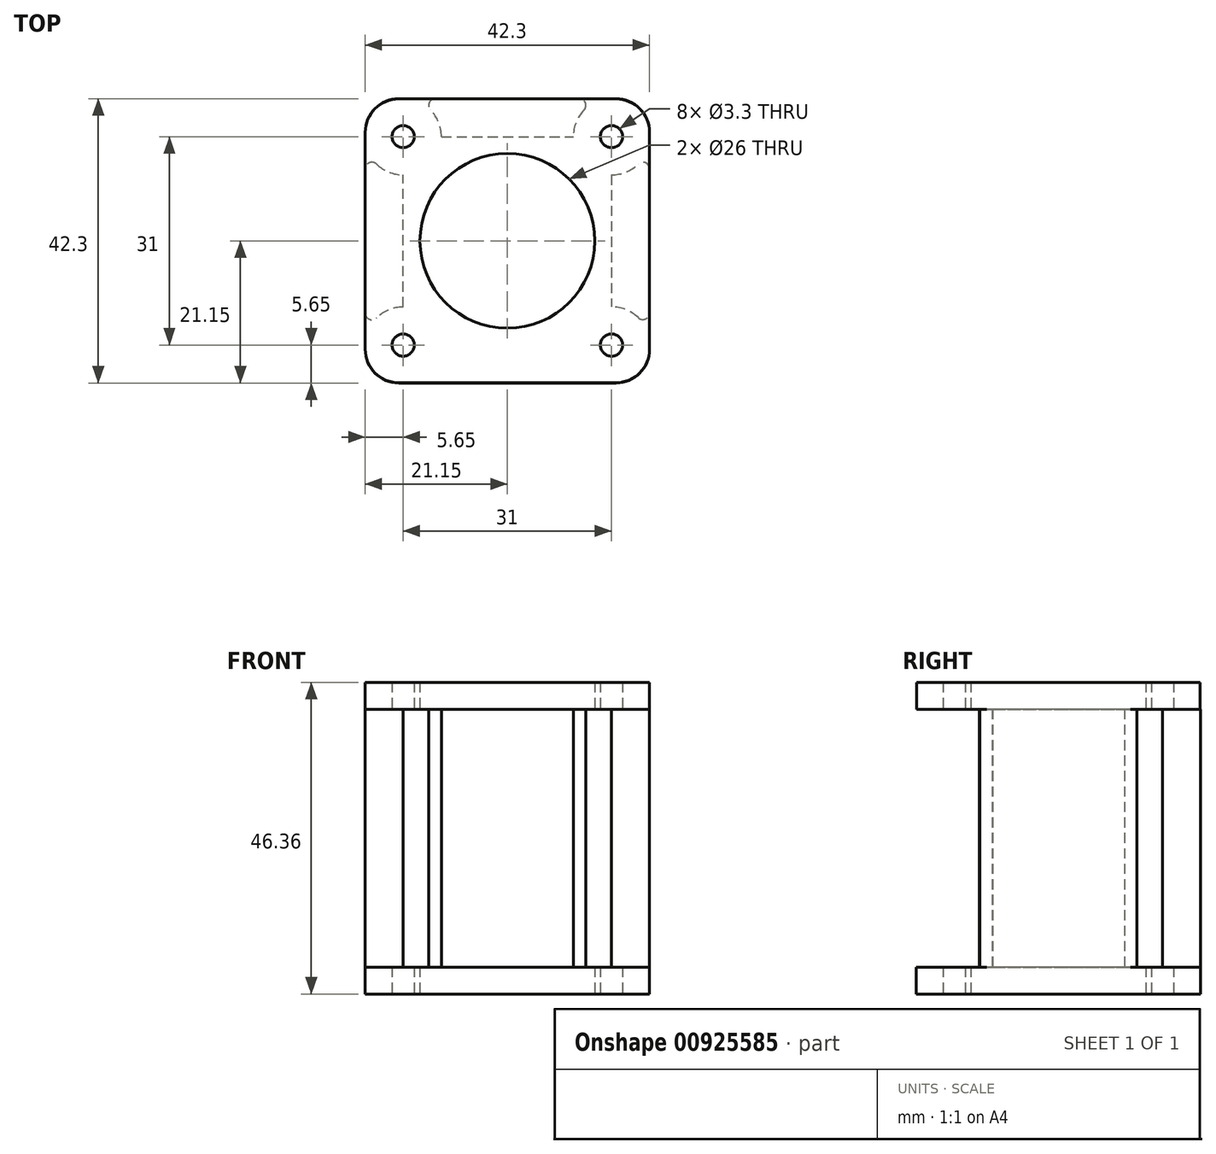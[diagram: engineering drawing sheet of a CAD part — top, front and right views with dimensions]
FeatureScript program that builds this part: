
annotation { "Feature Type Name" : "Feature", "Feature Type Description" : "" }
export const myFeature = defineFeature(function(context is Context, id is Id, definition is map)
    precondition{}
    {
        {
            var Q0;
            Q0=qCreatedBy(makeId("Top.planeOp"),FACE);
            var sketch = newSketch(context, id + "F0", { "sketchPlane" : qUnion([Q0])});
            skLineSegment(sketch, "E0.bottom", {"start": v(21.15, -21.15) * mm, "end": v(-21.15, -21.15) * mm});
            skLineSegment(sketch, "E0.top", {"start": v(21.15, 21.15) * mm, "end": v(-21.15, 21.15) * mm});
            skLineSegment(sketch, "E0.left", {"start": v(21.15, -21.15) * mm, "end": v(21.15, 21.15) * mm});
            skLineSegment(sketch, "E0.right", {"start": v(-21.15, -21.15) * mm, "end": v(-21.15, 21.15) * mm});
            skPoint(sketch, "E0.middle", {"position": v(0, 0) * mm});
            skCircle(sketch, "E1", {"center": v(-15.5, 15.5) * mm, "radius": 1.65 * mm});
            skCircle(sketch, "E2", {"center": v(15.5, 15.5) * mm, "radius": 1.65 * mm});
            skCircle(sketch, "E3", {"center": v(15.5, -15.5) * mm, "radius": 1.65 * mm});
            skCircle(sketch, "E4", {"center": v(-15.5, -15.5) * mm, "radius": 1.65 * mm});
            skCircle(sketch, "E5", {"center": v(0, 0) * mm, "radius": 13 * mm});
            skLineSegment(sketch, "E6", {"start": v(0, 10.82) * mm, "end": v(0, -11.36) * mm, "construction": true});
            skLineSegment(sketch, "E7", {"start": v(-9.37, 0) * mm, "end": v(8.86, 0) * mm, "construction": true});
            skSolve(sketch);
        }
        {
            var Q0;
            Q0 = qSketchRegion(id + "F0", true);
            extrude(context, id + "F1", {"entities" : qUnion([Q0]), "depth" : 4 * mm, "offsetDistance" : 25 * mm});
        }
        {
            var Q0;
            Q0=makeQuery(id+"F1.opExtrude","SWEPT_EDGE",EDGE,{"disambiguationData":[OSD([sQuery(id+"F0.wireOp",EDGE,"E0.bottom"),sQuery(id+"F0.wireOp",EDGE,"E0.right")])]});
            var Q1;
            Q1=makeQuery(id+"F1.opExtrude","SWEPT_EDGE",EDGE,{"disambiguationData":[OSD([sQuery(id+"F0.wireOp",EDGE,"E0.bottom"),sQuery(id+"F0.wireOp",EDGE,"E0.left")])]});
            var Q2;
            Q2=makeQuery(id+"F1.opExtrude","SWEPT_EDGE",EDGE,{"disambiguationData":[OSD([sQuery(id+"F0.wireOp",EDGE,"E0.top"),sQuery(id+"F0.wireOp",EDGE,"E0.right")])]});
            var Q3;
            Q3=makeQuery(id+"F1.opExtrude","SWEPT_EDGE",EDGE,{"disambiguationData":[OSD([sQuery(id+"F0.wireOp",EDGE,"E0.top"),sQuery(id+"F0.wireOp",EDGE,"E0.left")])]});
            fillet(context, id + "F2", {"entities" : qUnion([Q0, Q1, Q2, Q3]), "tangentPropagation" : true, "radius" : 5 * mm, "defaultsChanged" : false, "vertexSettings" : [], "allowEdgeOverflow" : false});
        }
        {
            var Q0;
            Q0=makeQuery(id+"F1.opExtrude","CAP_FACE",FACE,{"disambiguationData":[OSD([sQuery(id+"F0.wireOp",EDGE,"E0.bottom"),sQuery(id+"F0.wireOp",EDGE,"E0.top"),sQuery(id+"F0.wireOp",EDGE,"E0.left"),sQuery(id+"F0.wireOp",EDGE,"E0.right"),sQuery(id+"F0.wireOp",EDGE,"E1"),sQuery(id+"F0.wireOp",EDGE,"E2"),sQuery(id+"F0.wireOp",EDGE,"E3"),sQuery(id+"F0.wireOp",EDGE,"E4"),sQuery(id+"F0.wireOp",EDGE,"E5")])],"isStart":false});
            var sketch = newSketch(context, id + "F3", { "sketchPlane" : qUnion([Q0])});
            skArc(sketch, "E8", {"start": v(-19.45, 11.41) * mm, "mid": v(-17.63, 10.23) * mm, "end": v(-15.5, 9.81) * mm});
            skArc(sketch, "E9", {"start": v(11.41, 19.45) * mm, "mid": v(10.23, 17.63) * mm, "end": v(9.81, 15.5) * mm});
            skArc(sketch, "E10", {"start": v(19.45, -11.41) * mm, "mid": v(17.63, -10.23) * mm, "end": v(15.5, -9.81) * mm});
            skArc(sketch, "E11", {"start": v(-15.5, -9.85) * mm, "mid": v(-17.63, -10.27) * mm, "end": v(-19.45, -11.46) * mm});
            skLineSegment(sketch, "E12", {"start": v(-15.5, -9.85) * mm, "end": v(-15.5, 9.81) * mm});
            skLineSegment(sketch, "E13", {"start": v(-9.81, 15.5) * mm, "end": v(9.81, 15.5) * mm});
            skLineSegment(sketch, "E14", {"start": v(15.5, 9.81) * mm, "end": v(15.5, -9.81) * mm});
            skLineSegment(sketch, "E15.0", {"start": v(10.7, 21.15) * mm, "end": v(-10.7, 21.15) * mm});
            skLineSegment(sketch, "E16.0", {"start": v(-21.15, -10.75) * mm, "end": v(-21.15, 10.7) * mm});
            skLineSegment(sketch, "E17.0", {"start": v(21.15, -10.7) * mm, "end": v(21.15, 10.7) * mm});
            skArc(sketch, "E18.trimOffspring", {"start": v(-9.81, 15.5) * mm, "mid": v(-10.23, 17.63) * mm, "end": v(-11.41, 19.45) * mm});
            skArc(sketch, "E19.trimOffspring", {"start": v(15.5, 9.81) * mm, "mid": v(17.63, 10.23) * mm, "end": v(19.45, 11.41) * mm});
            skPoint(sketch, "E20.visualSharp", {"position": v(-14.85, 21.15) * mm});
            skArc(sketch, "E20.filletArc", {"start": v(-10.7, 21.15) * mm, "mid": v(-11.61, 20.54) * mm, "end": v(-11.41, 19.45) * mm});
            skPoint(sketch, "E21.visualSharp", {"position": v(-21.15, 14.85) * mm});
            skArc(sketch, "E21.filletArc", {"start": v(-19.45, 11.41) * mm, "mid": v(-20.54, 11.61) * mm, "end": v(-21.15, 10.7) * mm});
            skPoint(sketch, "E22.visualSharp", {"position": v(14.85, 21.15) * mm});
            skArc(sketch, "E22.filletArc", {"start": v(11.41, 19.45) * mm, "mid": v(11.61, 20.54) * mm, "end": v(10.7, 21.15) * mm});
            skPoint(sketch, "E23.visualSharp", {"position": v(21.15, 14.85) * mm});
            skArc(sketch, "E23.filletArc", {"start": v(21.15, 10.7) * mm, "mid": v(20.54, 11.61) * mm, "end": v(19.45, 11.41) * mm});
            skPoint(sketch, "E24.visualSharp", {"position": v(21.15, -14.85) * mm});
            skArc(sketch, "E24.filletArc", {"start": v(19.45, -11.41) * mm, "mid": v(20.54, -11.61) * mm, "end": v(21.15, -10.7) * mm});
            skPoint(sketch, "E25.visualSharp", {"position": v(-21.15, -15.5) * mm});
            skArc(sketch, "E25.filletArc", {"start": v(-21.15, -10.75) * mm, "mid": v(-20.54, -11.67) * mm, "end": v(-19.45, -11.46) * mm});
            skSolve(sketch);
        }
        {
            var Q0;
            Q0 = qSketchRegion(id + "F3", true);
            extrude(context, id + "F4", {"entities" : qUnion([Q0]), "operationType" : NewBodyOperationType.ADD, "depth" : 38.36 * mm, "offsetDistance" : 25 * mm});
        }
        {
            var Q0;
            Q0=makeQuery(id+"F4.opExtrude","CAP_FACE",FACE,{"disambiguationData":[OSD([sQuery(id+"F3.wireOp",EDGE,"E10"),sQuery(id+"F3.wireOp",EDGE,"E14"),sQuery(id+"F3.wireOp",EDGE,"E17.0"),sQuery(id+"F3.wireOp",EDGE,"E19.trimOffspring"),sQuery(id+"F3.wireOp",EDGE,"E23.filletArc"),sQuery(id+"F3.wireOp",EDGE,"E24.filletArc")])],"isStart":false});
            var sketch = newSketch(context, id + "F5", { "sketchPlane" : qUnion([Q0])});
            skLineSegment(sketch, "E26.bottom", {"start": v(21.15, -21.1) * mm, "end": v(-21.15, -21.1) * mm});
            skLineSegment(sketch, "E26.top", {"start": v(21.15, 21.1) * mm, "end": v(-21.15, 21.1) * mm});
            skLineSegment(sketch, "E26.left", {"start": v(21.15, -21.1) * mm, "end": v(21.15, 21.1) * mm});
            skLineSegment(sketch, "E26.right", {"start": v(-21.15, -21.1) * mm, "end": v(-21.15, 21.1) * mm});
            skPoint(sketch, "E26.middle", {"position": v(0, 0) * mm});
            skCircle(sketch, "E27.0", {"center": v(-15.5, 15.5) * mm, "radius": 1.65 * mm});
            skCircle(sketch, "E28.0", {"center": v(15.5, 15.5) * mm, "radius": 1.65 * mm});
            skCircle(sketch, "E29.0", {"center": v(15.5, -15.5) * mm, "radius": 1.65 * mm});
            skCircle(sketch, "E30.0", {"center": v(-15.5, -15.5) * mm, "radius": 1.65 * mm});
            skCircle(sketch, "E31.0", {"center": v(0, 0) * mm, "radius": 13 * mm});
            skSolve(sketch);
        }
        {
            var Q0;
            Q0 = qSketchRegion(id + "F5", true);
            extrude(context, id + "F6", {"entities" : qUnion([Q0]), "operationType" : NewBodyOperationType.ADD, "depth" : 4 * mm, "offsetDistance" : 25 * mm});
        }
        {
            var Q0;
            Q0=makeQuery(id+"F6.opExtrude","SWEPT_EDGE",EDGE,{"disambiguationData":[OSD([sQuery(id+"F5.wireOp",EDGE,"E26.bottom"),sQuery(id+"F5.wireOp",EDGE,"E26.right")])]});
            var Q1;
            Q1=makeQuery(id+"F6.opExtrude","SWEPT_EDGE",EDGE,{"disambiguationData":[OSD([sQuery(id+"F5.wireOp",EDGE,"E26.bottom"),sQuery(id+"F5.wireOp",EDGE,"E26.left")])]});
            var Q2;
            Q2=makeQuery(id+"F6.opExtrude","SWEPT_EDGE",EDGE,{"disambiguationData":[OSD([sQuery(id+"F5.wireOp",EDGE,"E26.top"),sQuery(id+"F5.wireOp",EDGE,"E26.right")])]});
            var Q3;
            Q3=makeQuery(id+"F6.opExtrude","SWEPT_EDGE",EDGE,{"disambiguationData":[OSD([sQuery(id+"F5.wireOp",EDGE,"E26.top"),sQuery(id+"F5.wireOp",EDGE,"E26.left")])]});
            fillet(context, id + "F7", {"entities" : qUnion([Q0, Q1, Q2, Q3]), "tangentPropagation" : true, "radius" : 5 * mm, "defaultsChanged" : false, "vertexSettings" : [], "allowEdgeOverflow" : false});
        }
    });
